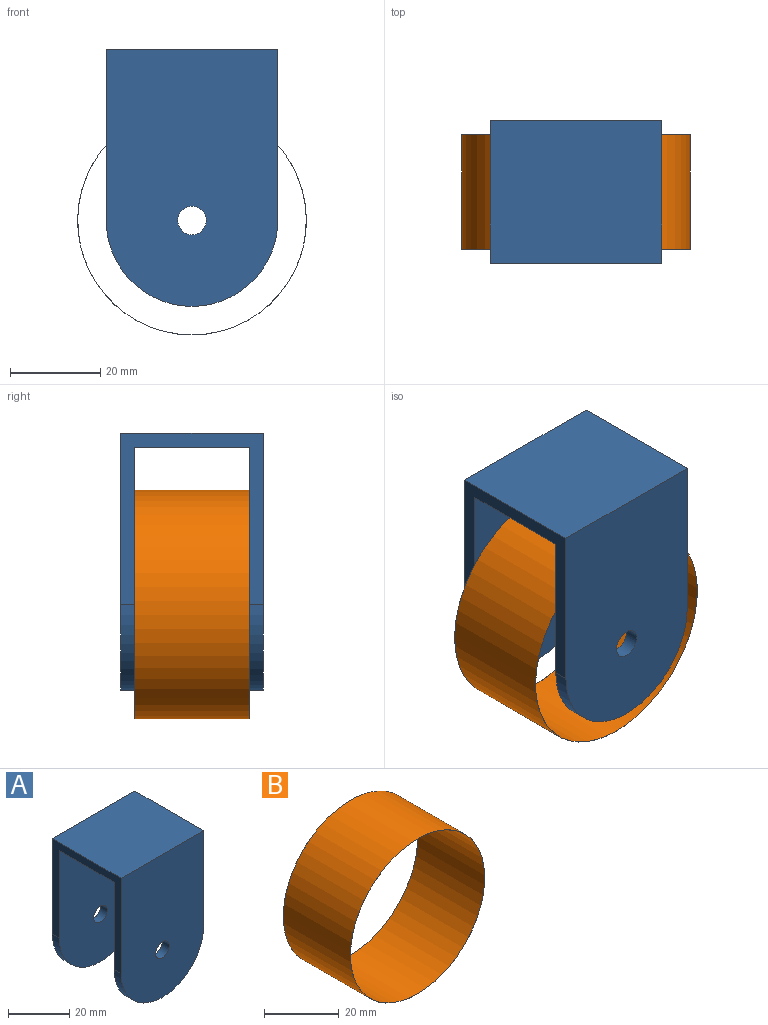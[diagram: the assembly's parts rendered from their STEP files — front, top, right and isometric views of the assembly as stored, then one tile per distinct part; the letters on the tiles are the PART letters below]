
ASSEMBLY  parts=2 mates=1
PART A: 12 faces, bbox 38.1x31.8x57.2 mm
  f0: cylinder r=19.05mm len=38.1mm, axis (0,1,0), area 190mm2, adj f1,f3,f6,f8
  f1: plane 38.1x31.75mm, normal (-1,0,0), area 322.6mm2, adj f0,f2,f4,f5,f6,f7,f8,f9
  f2: cylinder r=19.05mm len=38.1mm, axis (0,1,0), area 190mm2, adj f1,f3,f5,f7
  f3: plane 38.1x31.75mm, normal (1,0,0), area 322.6mm2, adj f0,f2,f4,f5,f6,f7,f8,f9
  f4: plane 38.1x31.75mm, normal (0,0,1), area 1209.7mm2, adj f1,f3,f5,f6
  f5: plane 57.15x38.1mm, normal (0,-1,0), area 1990mm2, adj f1,f2,f3,f4,f11
  f6: plane 57.15x38.1mm, normal (0,1,0), area 1990mm2, adj f0,f1,f3,f4,f10
  f7: plane 53.98x38.1mm, normal (0,1,0), area 1869mm2, adj f1,f2,f3,f9,f11
  f8: plane 53.98x38.1mm, normal (0,-1,0), area 1869mm2, adj f0,f1,f3,f9,f10
  f9: plane 38.1x25.4mm, normal (0,0,-1), area 967.7mm2, adj f1,f3,f7,f8
  f10: cylinder r=3.17mm len=6.35mm, axis (0,-1,0), area 63.3mm2, adj f6,f8
  f11: cylinder r=3.17mm len=6.35mm, axis (0,-1,0), area 63.3mm2, adj f5,f7
PART B: 4 faces, bbox 50.8x25.4x50.8 mm
  f0: cylinder r=25.37mm len=50.75mm, axis (0,1,0), area 4049.6mm2, adj f2,f3
  f1: cylinder r=25.4mm len=50.8mm, axis (0,1,0), area 4053.7mm2, adj f2,f3
  f2: plane 50.8x50.8mm, normal (0,-1,0), area 4.1mm2, adj f0,f1
  f3: plane 50.8x50.8mm, normal (0,1,0), area 4.1mm2, adj f0,f1
PLACE A t=(-9.31,65.43,-8.3)mm
PLACE B t=(-9.31,62.26,-8.3)mm
MATE revolute A.f0 <-> B.f1  axis (0,1,0) through (-9.31,36.86,-8.3)mm
